FCSTD DOCUMENT  (FreeCAD 0.16R5750 (Git))
Label: sketch-tutorial
License: All rights reserved
LicenseURL: http://en.wikipedia.org/wiki/All_rights_reserved
objects: Sketcher::SketchObject×1
note: 1 computed .brp shape members not serialized (recipe doc carries the construction recipe); baked Part::Feature solids carry a one-line shape summary decoded from their .brp

FEATURE [Sketcher::SketchObject] Sketch
  sketch-geometry (16):
    g0: LineSegment [constr] StartX=0 StartY=0 StartZ=0 EndX=29.815 EndY=9.68748 EndZ=0
    g1: LineSegment [constr] StartX=0 StartY=0 StartZ=0 EndX=18.4267 EndY=-25.3621 EndZ=0
    g2: LineSegment [constr] StartX=0 StartY=0 StartZ=0 EndX=-18.4267 EndY=-25.3621 EndZ=0
    g3: LineSegment [constr] StartX=0 StartY=0 StartZ=0 EndX=-29.815 EndY=9.68748 EndZ=0
    g4: LineSegment [constr] StartX=0 StartY=0 StartZ=0 EndX=0 EndY=31.3493 EndZ=0
    g5: Circle CenterX=0 CenterY=0 CenterZ=0 NormalX=0 NormalY=0 NormalZ=1 Radius=32.3496
    g6: ArcOfCircle CenterX=29.815 CenterY=9.68748 CenterZ=0 NormalX=0 NormalY=0 NormalZ=1 Radius=10.238 StartAngle=5.71019 EndAngle=7.44414
    g7: ArcOfCircle CenterX=0 CenterY=31.3493 CenterZ=0 NormalX=0 NormalY=0 NormalZ=1 Radius=10.238 StartAngle=0.642119 EndAngle=2.56203
    g8: ArcOfCircle CenterX=-18.4267 CenterY=-25.3621 CenterZ=0 NormalX=0 NormalY=0 NormalZ=1 Radius=10.238 StartAngle=2.60553 EndAngle=5.94558
    g9: ArcOfCircle CenterX=18.4267 CenterY=-25.3621 CenterZ=0 NormalX=0 NormalY=0 NormalZ=1 Radius=10.238 StartAngle=3.4792 EndAngle=6.78927
    g10: ArcOfCircle CenterX=42.0723 CenterY=-12.2571 CenterZ=0 NormalX=0 NormalY=0 NormalZ=1 Radius=16.7964 StartAngle=1.79013 EndAngle=3.64767
    g11: ArcOfCircle CenterX=0 CenterY=-31.8307 CenterZ=0 NormalX=0 NormalY=0 NormalZ=1 Radius=9.29111 StartAngle=0.337606 EndAngle=2.80399
    g12: ArcOfCircle CenterX=-29.815 CenterY=9.68748 CenterZ=0 NormalX=0 NormalY=0 NormalZ=1 Radius=8.1232 StartAngle=1.81844 EndAngle=3.69052
    g13: ArcOfCircle CenterX=19.3566 CenterY=25.9195 CenterZ=0 NormalX=0 NormalY=0 NormalZ=1 Radius=16.0674 StartAngle=2.33844 EndAngle=5.84331
    g14: ArcOfCircle CenterX=-18.3806 CenterY=25.0959 CenterZ=0 NormalX=0 NormalY=0 NormalZ=1 Radius=15.3945 StartAngle=3.65292 EndAngle=7.16269
    g15: ArcOfCircle CenterX=-27.8711 CenterY=-5.8111 CenterZ=0 NormalX=0 NormalY=0 NormalZ=1 Radius=14.3363 StartAngle=4.75723 EndAngle=8.5214
  constraints (30):
    c: Coincident(g0,g-1)
    c: Coincident(g1,g-1)
    c: Coincident(g2,g-1)
    c: Coincident(g3,g-1)
    c: Coincident(g4,g-1)
    c: Coincident(g5,g-1)
    c: Coincident(g6,g0)
    c: Coincident(g7,g4)
    c: Coincident(g8,g2)
    c: Coincident(g9,g1)
    c: Coincident(g10,g6)
    c: Coincident(g10,g9)
    c: Coincident(g11,g8)
    c: Coincident(g11,g9)
    c: Vertical(g4)  'Verticality'
    c: Coincident(g12,g3)
    c: Angle(g0,g4) = 1.25664
    c: Angle(g1,g0) = 1.25664
    c: Angle(g2,g1) = 1.25664
    c: Angle(g3,g2) = 1.25664
    c: Coincident(g13,g6)
    c: Coincident(g13,g7)
    c: Coincident(g14,g7)
    c: Coincident(g14,g12)
    c: Coincident(g15,g8)
    c: Coincident(g15,g12)
    c: Equal(g0,g1)
    c: Equal(g1,g2)
    c: Equal(g2,g3)
    c: Equal(g3,g4)
